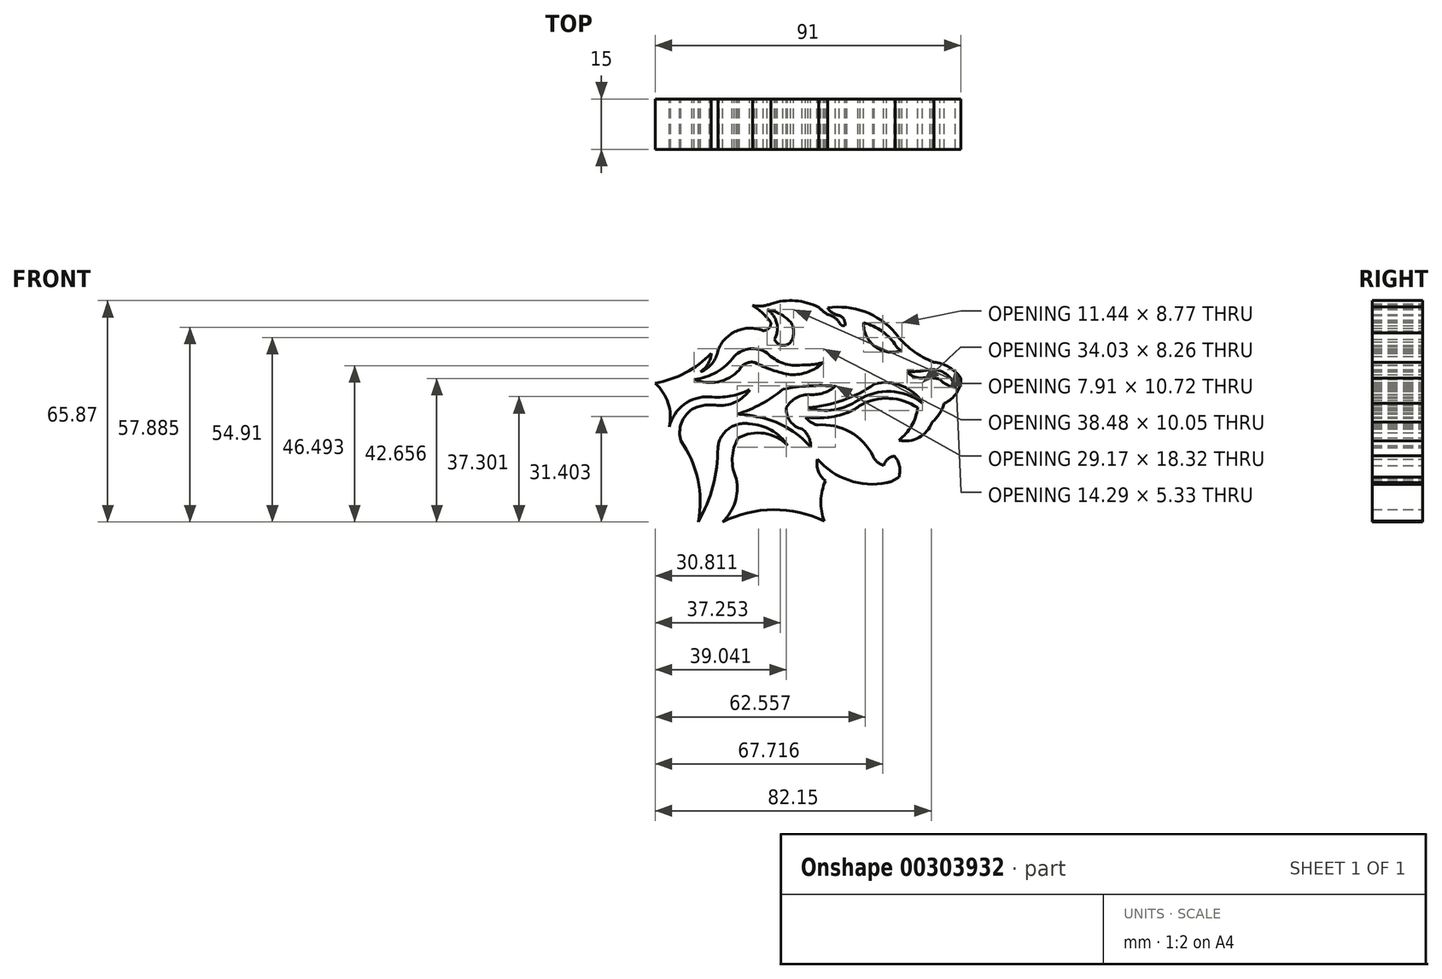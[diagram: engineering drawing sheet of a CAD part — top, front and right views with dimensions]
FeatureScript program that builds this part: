
annotation { "Feature Type Name" : "Feature", "Feature Type Description" : "" }
export const myFeature = defineFeature(function(context is Context, id is Id, definition is map)
    precondition{}
    {
        {
            var Q0;
            Q0=qCreatedBy(makeId("Front.planeOp"),FACE);
            var sketch = newSketch(context, id + "F0", { "sketchPlane" : qUnion([Q0])});
            skArc(sketch, "E0", {"start": v(6.6, -35.16) * mm, "mid": v(-8.54, -31.73) * mm, "end": v(-23.63, -35.34) * mm});
            skArc(sketch, "E1", {"start": v(6.94, -23.14) * mm, "mid": v(5.58, -29.12) * mm, "end": v(6.6, -35.16) * mm});
            skArc(sketch, "E2", {"start": v(4.56, -16.7) * mm, "mid": v(4.81, -20.26) * mm, "end": v(6.94, -23.14) * mm});
            skArc(sketch, "E3", {"start": v(4.56, -16.7) * mm, "mid": v(13.92, -22.97) * mm, "end": v(25.17, -23.72) * mm});
            skArc(sketch, "E4", {"start": v(25.17, -23.72) * mm, "mid": v(27.08, -23.06) * mm, "end": v(28.8, -21.98) * mm});
            skArc(sketch, "E5", {"start": v(21.13, -15.8) * mm, "mid": v(14.26, -8.58) * mm, "end": v(4.5, -6.52) * mm});
            skArc(sketch, "E6", {"start": v(0.98, -4.19) * mm, "mid": v(2.56, -5.63) * mm, "end": v(4.5, -6.52) * mm});
            skArc(sketch, "E7", {"start": v(0.98, -4.19) * mm, "mid": v(7.26, -4.3) * mm, "end": v(13.38, -2.9) * mm});
            skArc(sketch, "E8", {"start": v(13.38, -2.9) * mm, "mid": v(15.4, -1.93) * mm, "end": v(17.24, -0.67) * mm});
            skArc(sketch, "E9", {"start": v(34.4, -1.36) * mm, "mid": v(25.92, 1.4) * mm, "end": v(17.24, -0.67) * mm});
            skArc(sketch, "E10", {"start": v(28.8, -21.98) * mm, "mid": v(28.95, -18.66) * mm, "end": v(27.4, -15.72) * mm});
            skArc(sketch, "E11", {"start": v(27.4, -15.72) * mm, "mid": v(25.44, -16.7) * mm, "end": v(24.26, -18.54) * mm});
            skArc(sketch, "E12", {"start": v(21.13, -15.8) * mm, "mid": v(22.37, -17.55) * mm, "end": v(24.26, -18.54) * mm});
            skArc(sketch, "E13", {"start": v(28.8, -11.09) * mm, "mid": v(32.56, -6.78) * mm, "end": v(34.4, -1.36) * mm});
            skArc(sketch, "E14", {"start": v(28.8, -11.09) * mm, "mid": v(34.74, -10.24) * mm, "end": v(38.67, -5.7) * mm});
            skArc(sketch, "E15", {"start": v(38.67, -5.7) * mm, "mid": v(40.9, -3.11) * mm, "end": v(42.31, 0) * mm});
            skArc(sketch, "E16", {"start": v(42.31, 0) * mm, "mid": v(45.93, 2.98) * mm, "end": v(47.28, 7.47) * mm});
            skArc(sketch, "E17", {"start": v(47.28, 7.47) * mm, "mid": v(43.76, 10.67) * mm, "end": v(39.25, 12.2) * mm});
            skArc(sketch, "E18", {"start": v(27.74, 20.89) * mm, "mid": v(32.84, 15.67) * mm, "end": v(39.25, 12.2) * mm});
            skArc(sketch, "E19", {"start": v(27.74, 20.89) * mm, "mid": v(18.63, 27.2) * mm, "end": v(7.6, 28.34) * mm});
            skArc(sketch, "E20", {"start": v(7.6, 28.34) * mm, "mid": v(9.08, 26.81) * mm, "end": v(11.09, 26.1) * mm});
            skArc(sketch, "E21", {"start": v(12.74, 23.13) * mm, "mid": v(12.44, 24.9) * mm, "end": v(11.09, 26.1) * mm});
            skArc(sketch, "E22", {"start": v(11.09, 23.95) * mm, "mid": v(11.74, 23.2) * mm, "end": v(12.74, 23.13) * mm});
            skArc(sketch, "E23", {"start": v(11.09, 23.95) * mm, "mid": v(9.68, 25.46) * mm, "end": v(7.8, 26.3) * mm});
            skArc(sketch, "E24", {"start": v(4.99, 28.5) * mm, "mid": v(6.31, 27.3) * mm, "end": v(7.8, 26.3) * mm});
            skArc(sketch, "E25", {"start": v(4.99, 28.5) * mm, "mid": v(-2.03, 30.48) * mm, "end": v(-9.26, 29.57) * mm});
            skArc(sketch, "E26", {"start": v(-14.73, 29.08) * mm, "mid": v(-11.96, 28.92) * mm, "end": v(-9.26, 29.57) * mm});
            skArc(sketch, "E27", {"start": v(-9.26, 23.95) * mm, "mid": v(-11.73, 26.8) * mm, "end": v(-14.73, 29.08) * mm});
            skArc(sketch, "E28", {"start": v(-11.58, 21.58) * mm, "mid": v(-9.92, 22.28) * mm, "end": v(-9.26, 23.95) * mm});
            skArc(sketch, "E29", {"start": v(-11.58, 21.58) * mm, "mid": v(-19.57, 21.45) * mm, "end": v(-25.08, 15.66) * mm});
            skArc(sketch, "E30", {"start": v(-30.26, 9.32) * mm, "mid": v(-26.8, 11.79) * mm, "end": v(-25.08, 15.66) * mm});
            skArc(sketch, "E31", {"start": v(-30.26, 9.32) * mm, "mid": v(-28.02, 11.66) * mm, "end": v(-27.03, 14.75) * mm});
            skArc(sketch, "E32", {"start": v(-43.72, 5.88) * mm, "mid": v(-34.7, 9.04) * mm, "end": v(-27.03, 14.75) * mm});
            skArc(sketch, "E33", {"start": v(-39.54, -7.16) * mm, "mid": v(-39.83, -0.06) * mm, "end": v(-43.72, 5.88) * mm});
            skArc(sketch, "E34", {"start": v(-27.52, 1.87) * mm, "mid": v(-35.2, -0.43) * mm, "end": v(-39.54, -7.16) * mm});
            skArc(sketch, "E35", {"start": v(-27.52, 1.87) * mm, "mid": v(-21.4, 2.07) * mm, "end": v(-15.6, 3.98) * mm});
            skArc(sketch, "E36", {"start": v(-24.7, -0.74) * mm, "mid": v(-19.54, 0.44) * mm, "end": v(-15.6, 3.98) * mm});
            skArc(sketch, "E37", {"start": v(-24.7, -0.74) * mm, "mid": v(-28.83, -0.62) * mm, "end": v(-32.78, -1.82) * mm});
            skArc(sketch, "E38", {"start": v(-32.78, -1.82) * mm, "mid": v(-35.95, -6.01) * mm, "end": v(-36.1, -11.26) * mm});
            skArc(sketch, "E39", {"start": v(-30.92, -35.33) * mm, "mid": v(-31.02, -22.76) * mm, "end": v(-36.1, -11.26) * mm});
            skArc(sketch, "E40", {"start": v(-30.92, -35.33) * mm, "mid": v(-26.53, -24.71) * mm, "end": v(-25.08, -13.32) * mm});
            skArc(sketch, "E41", {"start": v(-15.6, -6.17) * mm, "mid": v(-21.92, -7.65) * mm, "end": v(-25.08, -13.32) * mm});
            skArc(sketch, "E42", {"start": v(-4.3, -12.62) * mm, "mid": v(-9.18, -8.06) * mm, "end": v(-15.6, -6.17) * mm});
            skArc(sketch, "E43", {"start": v(-4.3, -12.62) * mm, "mid": v(-11.27, -9) * mm, "end": v(-19, -10.4) * mm});
            skArc(sketch, "E44", {"start": v(-19, -10.4) * mm, "mid": v(-20.78, -16.42) * mm, "end": v(-19.53, -22.57) * mm});
            skArc(sketch, "E45", {"start": v(-23.63, -35.34) * mm, "mid": v(-19.96, -29.48) * mm, "end": v(-19.53, -22.57) * mm});
            skArc(sketch, "E46", {"start": v(28, 16.9) * mm, "mid": v(23.84, 21.4) * mm, "end": v(18.27, 23.95) * mm});
            skArc(sketch, "E47", {"start": v(28, 16.9) * mm, "mid": v(28.75, 16.13) * mm, "end": v(29.72, 15.66) * mm});
            skArc(sketch, "E48", {"start": v(18.27, 23.95) * mm, "mid": v(21.79, 16.76) * mm, "end": v(29.72, 15.66) * mm});
            skArc(sketch, "E49", {"start": v(31.28, 9.32) * mm, "mid": v(34.7, 9.5) * mm, "end": v(38.08, 9.98) * mm});
            skArc(sketch, "E50", {"start": v(45.58, 4.65) * mm, "mid": v(42.8, 8.69) * mm, "end": v(38.08, 9.98) * mm});
            skArc(sketch, "E51", {"start": v(40.95, 7.11) * mm, "mid": v(43.06, 5.5) * mm, "end": v(45.58, 4.65) * mm});
            skArc(sketch, "E52", {"start": v(40.95, 7.11) * mm, "mid": v(38.42, 7.55) * mm, "end": v(35.85, 7.47) * mm});
            skArc(sketch, "E53", {"start": v(31.28, 9.32) * mm, "mid": v(33.34, 7.84) * mm, "end": v(35.85, 7.47) * mm});
            skArc(sketch, "E54", {"start": v(35.85, 0) * mm, "mid": v(29.62, 5.22) * mm, "end": v(21.5, 5.65) * mm});
            skArc(sketch, "E55", {"start": v(1.82, -1.38) * mm, "mid": v(12.13, 0.82) * mm, "end": v(21.5, 5.65) * mm});
            skArc(sketch, "E56", {"start": v(1.82, -1.38) * mm, "mid": v(9.46, -2) * mm, "end": v(16.58, 0.84) * mm});
            skArc(sketch, "E57", {"start": v(35.85, 0) * mm, "mid": v(26.35, 3.46) * mm, "end": v(16.58, 0.84) * mm});
            skArc(sketch, "E58", {"start": v(-19.26, -3.26) * mm, "mid": v(-12.11, -0.23) * mm, "end": v(-5.68, 4.12) * mm});
            skArc(sketch, "E59", {"start": v(9.9, 5.06) * mm, "mid": v(2.08, 5.12) * mm, "end": v(-5.68, 4.12) * mm});
            skArc(sketch, "E60", {"start": v(2.52, 2.54) * mm, "mid": v(6.46, 3.07) * mm, "end": v(9.9, 5.06) * mm});
            skArc(sketch, "E61", {"start": v(2.52, 2.54) * mm, "mid": v(-1.66, 1.6) * mm, "end": v(-4.74, -1.38) * mm});
            skArc(sketch, "E62", {"start": v(-4.74, -1.38) * mm, "mid": v(-3.55, -5.43) * mm, "end": v(0, -7.7) * mm});
            skArc(sketch, "E63", {"start": v(2.52, -13.1) * mm, "mid": v(1.94, -10.09) * mm, "end": v(0, -7.7) * mm});
            skArc(sketch, "E64", {"start": v(2.52, -13.1) * mm, "mid": v(-4.66, -7.15) * mm, "end": v(-13.47, -4.08) * mm});
            skArc(sketch, "E65", {"start": v(-13.47, -4.08) * mm, "mid": v(-16.34, -3.53) * mm, "end": v(-19.26, -3.26) * mm});
            skArc(sketch, "E66", {"start": v(-32.15, 7.11) * mm, "mid": v(-25.43, 9.24) * mm, "end": v(-20.2, 13.96) * mm});
            skArc(sketch, "E67", {"start": v(-10.42, 14.9) * mm, "mid": v(-15.48, 16.16) * mm, "end": v(-20.2, 13.96) * mm});
            skArc(sketch, "E68", {"start": v(-10.42, 14.9) * mm, "mid": v(-5.64, 11.88) * mm, "end": v(0, 11.39) * mm});
            skArc(sketch, "E69", {"start": v(0, 11.39) * mm, "mid": v(3.2, 11.5) * mm, "end": v(6.33, 12.15) * mm});
            skArc(sketch, "E70", {"start": v(-3.41, 8.46) * mm, "mid": v(1.84, 9.31) * mm, "end": v(6.33, 12.15) * mm});
            skArc(sketch, "E71", {"start": v(-14.1, 12.15) * mm, "mid": v(-8.92, 9.85) * mm, "end": v(-3.41, 8.46) * mm});
            skArc(sketch, "E72", {"start": v(-14.1, 12.15) * mm, "mid": v(-16.8, 11.77) * mm, "end": v(-18.74, 9.86) * mm});
            skArc(sketch, "E73", {"start": v(-32.15, 7.11) * mm, "mid": v(-25, 6.36) * mm, "end": v(-18.74, 9.86) * mm});
            skArc(sketch, "E74", {"start": v(-3.41, 24.16) * mm, "mid": v(-6.63, 26.56) * mm, "end": v(-10.42, 27.9) * mm});
            skArc(sketch, "E75", {"start": v(-3.41, 18.18) * mm, "mid": v(-2.51, 21.17) * mm, "end": v(-3.41, 24.16) * mm});
            skArc(sketch, "E76", {"start": v(-8.25, 19.06) * mm, "mid": v(-6.09, 17.22) * mm, "end": v(-3.41, 18.18) * mm});
            skArc(sketch, "E77", {"start": v(-8.25, 19.06) * mm, "mid": v(-7.35, 21.82) * mm, "end": v(-7.84, 24.68) * mm});
            skArc(sketch, "E78", {"start": v(-7.84, 24.68) * mm, "mid": v(-8.88, 26.5) * mm, "end": v(-10.42, 27.9) * mm});
            skSolve(sketch);
        }
        {
            var Q0;
            Q0 = qSketchRegion(id + "F0", true);
            extrude(context, id + "F1", {"entities" : qUnion([Q0]), "depth" : 15 * mm});
        }
    });
